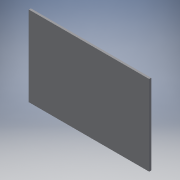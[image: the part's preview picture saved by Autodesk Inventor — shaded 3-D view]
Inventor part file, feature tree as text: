
AUTODESK INVENTOR PART (.ipt)
format: ipt  version: 2016 (Build 200138000, 138)  size: 90,112 bytes
history: native  units: mm
features: other x1, extrude x1, sketch x1
ambient origin geometry x8: Origin, YZ Plane, XZ Plane, XY Plane, X Axis, Y Axis, Z Axis, Center Point
bodies: Solid1 (feature_tree)
feature tree (3):
  parser-record x1  (decoder bookkeeping rows leaked as tree rows — omitted from the tree; the rows remain in map.json)
  extrude  "Extrusion1"  [1 undecoded]
  sketch  "Sketch1"  dims[d3=0.0mm]
note: 1 required parameter value undecoded (feature->parameter linkage not recoverable at this tier; creation-order binding heuristic only, values carry confidence <= 0.55)
note: 1 file-system path scrubbed to <path> (originals preserved in map.json)
